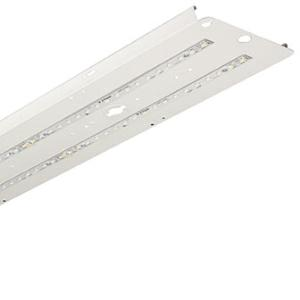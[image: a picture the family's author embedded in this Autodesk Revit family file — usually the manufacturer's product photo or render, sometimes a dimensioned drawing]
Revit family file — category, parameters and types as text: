
# Revit family: 3f_filippi_-_kit_led_retrofit_per_schermo_in_vetro_3f_filippi_-_a5117_a5184_-_kit_led_i3f_76__a3f_91_-_l_fe5811b4c37595fa
name_source: partatom
category: Lighting Fixtures
units: mm (PartAtom-declared; Revit-internal decimal feet)

## family parameters
Cut with Voids When Loaded = No
Host = Face
Light Source = No
Part Type = Normal
Room Calculation Point = No
Round Connector Dimension = Use Diameter
Shared = No

## types (1)
- 3F Filippi - Kit LED Retrofit per schermo in vetro (1 x LED, 8174 lm, 66 W, 4000 K)
    Apparent Load = 66 VA
    Approval mark = ENEC
    CIE Flux Codes = 62 90 98 100 100
    Color Rendering = 80
    Color Temperature = 4000 K
    Control Gear = Electronic ballast
    Default Elevation = 1800 mm
    Description = Led retrofit kit suitable for Fluorescent Beta 2x i3F 76 and A3F 91 luminaires.

ILLUMINOTECHNICAL
Luminous efficiency 100% (DLOR 100%, ULOR 0%).
Initial luminous flux of the luminaire 8174 lm.
Symmetric distribution.
Installation Interdistance Transv.D = 1.31 x hu - Long.D = 1.31 x hu.
Tabular UGR (CIE 117 - 4H-8H; S=0.25H; 70/50/20): RUG 19.5 - 20.8.
Beam angle: 90° - 99°.
Luminous efficacy 124 lm/W.
Lifetime (L93/B10): 30000 h. (tq+25°C)
Lifetime (L90/B10): 50000 h. (tq+25°C)
Lifetime (L85/B10): 80000 h. (tq+25°C)
Lifetime (L80/B10): 100000 h. (tq+25°C)
Lifetime (L85/B10): 50000 h. (tq+35°C)
Sudden decreased luminous flux after 50000 hours: 0% (C0).
Photobiological safety in compliance with IEC/TR 62778: RG0 risk exempt, (IEC 62471).
In compliance with IEC/EN 62722-2-1 - IEC/EN 62717 standards.

SOURCE
2 linear LED modules 30W/840.
Energy efficiency class (UE 2019/2020 - UE 2019/2015): D.
CIE 13.3 Colour rendering index: CRI >80 (R9 <50%).
IES TM-30 Fidelity Index: Rf = 84 Rg = 95.
CCT nominal colour temperature 4000 K.
Colour initial tolerance (MacAdam): SDCM 3.

MECHANICAL
Gear-tray unit in hot-galvanised steel, painted in white polyester, fixed to the housing by means of "Ribloc" rapid devices in galvanised steel, hinged opening.
Luminaire with limited surface temperature. - D - (EN 60598-2-24)
Dimensions: 1565x235 mm, height 105 mm. Weight 6.437 kg.
Glow-wire test resistance 850°C.

ELECTRICAL
Halogen Free electronic wiring 230V-50/60Hz, power factor 0.97, THD <25%, constant output current, SELV, class I, 1 driver.
Power of the luminaire 66 W.
CE - IEC 60598-1 - EN 60598-1.
SAFE FLICKER: PstLM=<1 and SVM=<0.4 (IEC TR 61547-1 and IEC TR 63158), to ensure a more comfortable and safe light.
Luminaire compliant with EN 60598-2-22 for power supply from a centralised emergency system CPSS (Central Power Supply System), not incorporated in the luminaire - high risk areas excluded. The default power and flux are 100% in AC and 100% in DC.
Ambient temperature from -20°C to +35°C.
Temperature class T6 max 85°C.
Relative humidity UR: <85%.

INSTALLATION
Retrofit.
Correct installation of the retrofit LED kit, compliant with EN 60598-1 and CE marked, inside the 3F Filippi - Beta 2x i3F 76, A3F 91 and A3F 93 Fluorescent luminaires must be only carried out by qualified personnel to ensure compliance with the national installation standards.
Attention: to maintain the degree of protection of the device and for the purposes of validity of the guarantee of the new retrofit kits, it is imperative to replace the old cable guides (on the body of the device) with the new ones supplied.
All accessories dedicated to this product are available on the Catalog and on our website www.3F-Filippi.com.

ACCESSORIES
A5184 - Printed glass Beta 2x i3F 76 - L1565.

WARNING
Fixture not suitable for cold stores with an ambient temperature <0°C and/or relative humidity >85%.
Luminaire designed for disposal/recycling at end-of-life.
Replaceable (LED only) light source by a professional. Replaceable control gear by a professional.
    Height = 105 mm
    Lamp = 1 x LED
    Lamp Light Flux = 8174 lm
    Lamp Power = 66 W
    Lamp count = 1
    Length = 1565 mm
    Lifetime = 50000 h
    Luminous efficacy = 124 lm/W
    Manufacturer = 3F Filippi
    ModVariant = No
    Model = 3F Filippi - A5117+A5184 - KIT LED i3F 76, A3F 91 - L1565-2x30W + VS
    Mounting Place = Ceiling
    Mounting Type = Surface mounted
    Number of Poles = 1
    OnlyDefault = Yes
    Power Factor = 1
    Product Name = 3F Filippi - Kit LED Retrofit per schermo in vetro
    Product group = ceiling mounted luminaire
    ProductGroupID = 3
    Protection Class = Protection class I
    Protection Degree = Degree of protection
    RLX_Detail_Level = 1
    RLX_Emergency_Light_Flux = 0 lm
    RLX_Emergency_Type = 0
    RLX_Emergency_Type_DB = No
    RlxData = <blob elided: 58393 chars, md5=bf1c834b>
    Socket = socket
    Standby Power = 0 W
    System Light Flux = 8174 lm
    System Power = 66 W
    Type Comments = Product without accessories
    Type Image = 3ffilippi_a5117_a5184.jpg
    URL = http://relux.com
    VarID = ---
    Voltage = 0 V
    Weight = 0.00 kg
    Width = 235 mm

## geometry (parser evidence)
native form markers: Blend x4, Sweep x10
no freeform markers — native parametric forms only
